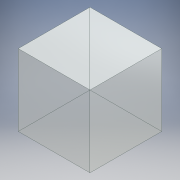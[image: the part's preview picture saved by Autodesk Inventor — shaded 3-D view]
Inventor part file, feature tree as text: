
AUTODESK INVENTOR PART (.ipt)
format: ipt  version: 2018.1 (Build 221171000, 171)  size: 92,672 bytes
history: native  units: mm
features: extrude x1, sketch x1
ambient origin geometry x8: Origin, YZ Plane, XZ Plane, XY Plane, X Axis, Y Axis, Z Axis, Center Point
bodies: Solid1 (feature_tree)
feature tree (2):
  extrude  "Extrusion1"  Depth=10.0mm
  sketch  "Sketch1"  dims[d0=10.0mm d1=0.0mm d2=10.0mm d3=10.0mm]
